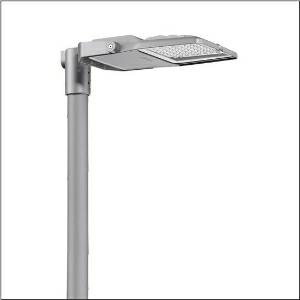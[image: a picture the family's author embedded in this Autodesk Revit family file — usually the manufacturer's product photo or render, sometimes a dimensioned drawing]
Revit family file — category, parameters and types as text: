
# Revit family: floodlight_fl_21_mini___pl52_5xa7775d2d3a_ca02
name_source: partatom
category: Lighting Fixtures
units: mm (PartAtom-declared; Revit-internal decimal feet)

## family parameters
Cut with Voids When Loaded = No
Host = Face
Light Source = No
Part Type = Normal
Room Calculation Point = No
Round Connector Dimension = Use Diameter
Shared = No

## types (1)
- --- (1 x LED, 17840 lm, 142.9 W, 3000K)
    Apparent Load = 143 VA
    CIE Flux Codes = 26 60 98 100 100
    Color Rendering = 70
    Color Temperature = 3000K
    Default Elevation = 1800 mm
    Description = Floodlight FL 21 mini, floodlight, primary light control with lens, of PMMA, primary optical cover: protective disc, of toughened safety glass, transparent, light distribution: PL52, light emission: direct distribution, installation type: surface-mounted, LED, High Power LED, rated luminous flux: 17.840lm, luminous efficacy: 125lm/W, light colour: 730, colour temperature: 3000K, control gear: Smart Interface (Zhaga), control: flexible luminous flux parameterisation, time-dependent luminous flux control, constant luminous flux control, overheat protection, pre-setting: logarithmic dimming characteristic, with terminal, 6-pole, mains connection: 220..240V, AC, 50/60Hz, start of lifetime: 143W, end of service life: 151W, reduction: 63W, luminaire housing, of diecast aluminium, powder-coated, Siteco® metallic grey (DB 702S), corrosivity category C5 mid according to DIN EN ISO 12944, suitable for swimming pools, chlorine-resistant, sealing non-destructively replaceable, please order mast flange separately, mast bracket, of steel, galvanised, powder-coated, Siteco® metallic grey (DB 702S), Smart Interface above, protection rating (complete): IP66, insulation class (complete): insulation class II (safety insulation), certification: CE, ENEC, VDE, protection symbol: D, impact resistance: IK08, permissible operating ambient temperature: -40..+40°C, permissible operating ambient temperature for outdoor applications: -40..+50°C, standard: DIN EN 12944, LABS conformity tested according to VDMA 24364:2018-05, packaging unit: 1 piece

Light Distribution: PL52
    Height = 70 mm
    Lamp = 1 x LED
    Lamp Light Flux = 17840 lm
    Lamp Power = 142.9 W
    Lamp count = 1
    Length = 485 mm
    Luminous efficacy = 125 lm/W
    Manufacturer = Siteco
    ModVariant = No
    Model = 5XA7775D2D3A
    Number of Poles = 1
    OnlyDefault = Yes
    Power Factor = 1
    Product Name = Floodlight FL 21 mini | PL52
    Product group = floodlight | pylon annexe
    ProductGroupID = 6201
    Protection Class = Protection class II
    Protection Degree = IP 66
    RLX_Detail_Level = 1
    RLX_Emergency_Light_Flux = 0 lm
    RLX_Emergency_Type = 0
    RLX_Emergency_Type_DB = No
    RlxData = <blob elided: 101589 chars, md5=9234cb3b>
    Socket = socket
    Standby Power = 0 W
    System Light Flux = 17840 lm
    System Power = 143 W
    Type Comments = factory setting: luminous flux: 100 % | dim-lin: 254 | 730 mA
    Type Image = l_1007125.jpg
    URL = http://relux.com
    VarID = @adj_184635
    Voltage = 0 V
    Weight = 0.00 kg
    Width = 337 mm

## geometry (parser evidence)
native form markers: Blend x4, Sweep x13
no freeform markers — native parametric forms only
